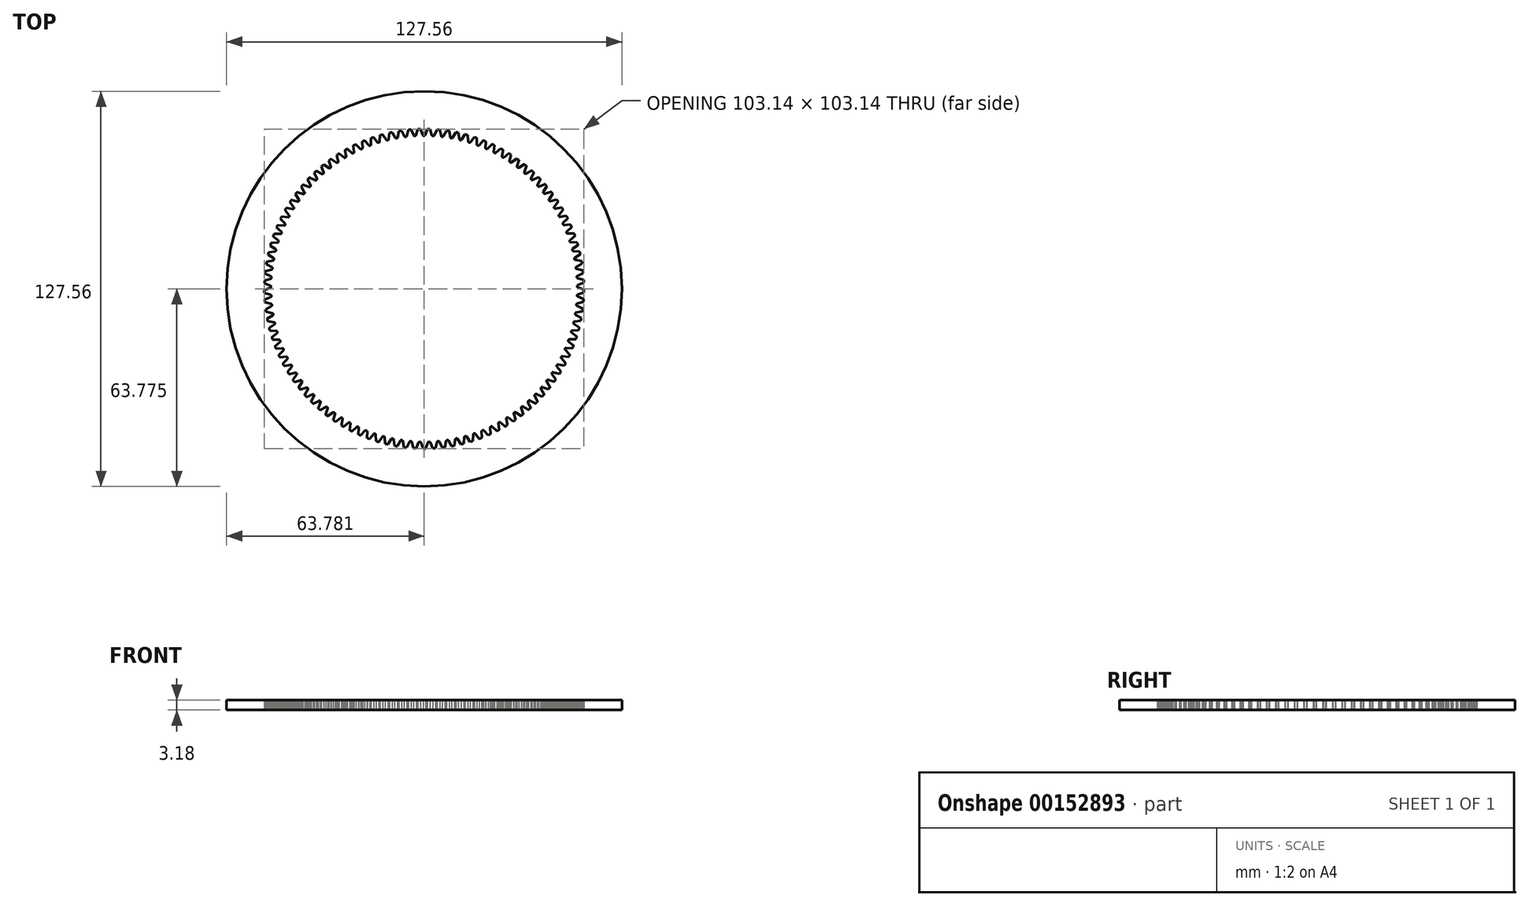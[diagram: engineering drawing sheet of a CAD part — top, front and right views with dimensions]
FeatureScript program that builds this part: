
annotation { "Feature Type Name" : "Feature", "Feature Type Description" : "" }
export const myFeature = defineFeature(function(context is Context, id is Id, definition is map)
    precondition{}
    {
        {
            var Q0;
            Q0=qCreatedBy(makeId("Top.planeOp"),FACE);
            var sketch = newSketch(context, id + "F0", { "sketchPlane" : qUnion([Q0])});
            skArc(sketch, "E0", {"start": v(2.79, 49.33) * mm, "mid": v(1.4, 49.4) * mm, "end": v(0, 49.41) * mm});
            skArc(sketch, "E1", {"start": v(0, 49.41) * mm, "mid": v(0.17, 49.46) * mm, "end": v(0.28, 49.6) * mm});
            skArc(sketch, "E2", {"start": v(2.52, 49.54) * mm, "mid": v(2.62, 49.4) * mm, "end": v(2.79, 49.33) * mm});
            skLineSegment(sketch, "E3", {"start": v(0.28, 49.6) * mm, "end": v(1.02, 51.56) * mm});
            skArc(sketch, "E4", {"start": v(1.9, 51.54) * mm, "mid": v(1.46, 51.55) * mm, "end": v(1.02, 51.56) * mm});
            skLineSegment(sketch, "E5", {"start": v(1.9, 51.54) * mm, "end": v(2.52, 49.54) * mm});
            skLineSegment(sketch, "E6", {"start": v(1.43, 50.56) * mm, "end": v(1.46, 51.55) * mm, "construction": true});
            skPoint(sketch, "E7", {"position": v(0.65, 50.58) * mm});
            skArc(sketch, "E8", {"start": v(1.02, 51.56) * mm, "mid": v(0.51, 51.57) * mm, "end": v(0, 51.57) * mm, "construction": true});
            skLineSegment(sketch, "E9", {"start": v(0.65, 50.58) * mm, "end": v(2.2, 50.54) * mm, "construction": true});
            skArc(sketch, "E10", {"start": v(0, 49.41) * mm, "mid": v(-1.4, -49.4) * mm, "end": v(2.79, 49.33) * mm});
            skCircle(sketch, "E11", {"center": v(0, 0) * mm, "radius": 63.78 * mm});
            skLineSegment(sketch, "E12", {"start": v(0, 0) * mm, "end": v(0, 49.41) * mm, "construction": true});
            skLineSegment(sketch, "E13", {"start": v(0, 49.41) * mm, "end": v(0, 51.57) * mm, "construction": true});
            skLineSegment(sketch, "E14", {"start": v(0.66, 51.57) * mm, "end": v(0, 0) * mm, "construction": true});
            skSolve(sketch);
        }
        {
            var Q0;
            Q0 = qSketchRegion(id + "F0", true);
            extrude(context, id + "F1", {"entities" : qUnion([Q0]), "depth" : 3.17 * mm});
        }
        {
            var Q0;
            Q0=makeQuery(id+"F1.opExtrude","SWEPT_FACE",FACE,{"disambiguationData":[OSD([sQuery(id+"F0.wireOp",EDGE,"E2")])]});
            var Q1;
            Q1=makeQuery(id+"F1.opExtrude","SWEPT_FACE",FACE,{"disambiguationData":[OSD([sQuery(id+"F0.wireOp",EDGE,"E5")])]});
            var Q2;
            Q2=makeQuery(id+"F1.opExtrude","SWEPT_FACE",FACE,{"disambiguationData":[OSD([sQuery(id+"F0.wireOp",EDGE,"E4")])]});
            var Q3;
            Q3=makeQuery(id+"F1.opExtrude","SWEPT_FACE",FACE,{"disambiguationData":[OSD([sQuery(id+"F0.wireOp",EDGE,"E3")])]});
            var Q4;
            Q4=makeQuery(id+"F1.opExtrude","SWEPT_FACE",FACE,{"disambiguationData":[OSD([sQuery(id+"F0.wireOp",EDGE,"E1")])]});
            var Q5;
            Q5=makeQuery(id+"F1.opExtrude","SWEPT_FACE",FACE,{"disambiguationData":[OSD([sQuery(id+"F0.wireOp",EDGE,"E10")])]});
            circularPattern(context, id + "F2", {"patternType" : PatternType.FACE, "faces" : qUnion([Q0, Q1, Q2, Q3, Q4]), "axis" : qUnion([Q5]), "angle" : 3.43 * degree, "instanceCount" : 105});
        }
    });
